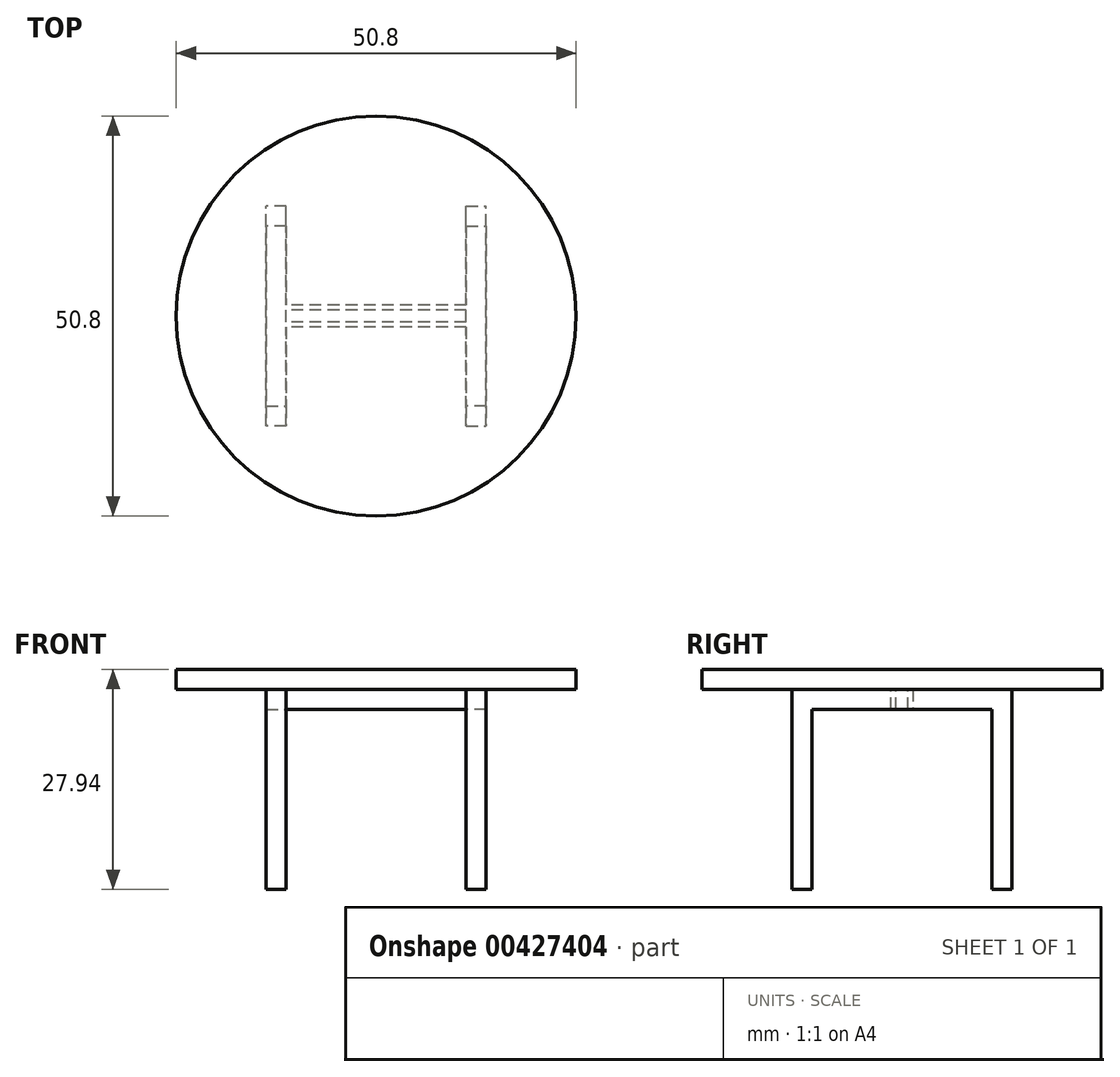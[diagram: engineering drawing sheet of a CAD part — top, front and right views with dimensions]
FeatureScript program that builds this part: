
annotation { "Feature Type Name" : "Feature", "Feature Type Description" : "" }
export const myFeature = defineFeature(function(context is Context, id is Id, definition is map)
    precondition{}
    {
        {
            var Q0;
            Q0=qCreatedBy(makeId("Top.planeOp"),FACE);
            var sketch = newSketch(context, id + "F0", { "sketchPlane" : qUnion([Q0])});
            skCircle(sketch, "E0", {"center": v(0, 0) * mm, "radius": 25.4 * mm});
            skSolve(sketch);
        }
        {
            var Q0;
            Q0 = qSketchRegion(id + "F0", true);
            extrude(context, id + "F1", {"entities" : qUnion([Q0]), "depth" : 2.54 * mm});
        }
        {
            var Q0;
            Q0=makeQuery(id+"F1.opExtrude","CAP_FACE",FACE,{"disambiguationData":[OSD([sQuery(id+"F0.wireOp",EDGE,"E0")])],"isStart":true});
            var sketch = newSketch(context, id + "F2", { "sketchPlane" : qUnion([Q0])});
            skLineSegment(sketch, "E1.bottom", {"start": v(11.43, -11.43) * mm, "end": v(13.97, -11.43) * mm});
            skLineSegment(sketch, "E1.top", {"start": v(11.43, -13.97) * mm, "end": v(13.97, -13.97) * mm});
            skLineSegment(sketch, "E1.left", {"start": v(11.43, -11.43) * mm, "end": v(11.43, -13.97) * mm});
            skLineSegment(sketch, "E1.right", {"start": v(13.97, -11.43) * mm, "end": v(13.97, -13.97) * mm});
            skPoint(sketch, "E1.middle", {"position": v(12.7, -12.7) * mm});
            skLineSegment(sketch, "E2.MirrorCS", {"start": v(-11.43, -13.97) * mm, "end": v(-13.97, -13.97) * mm});
            skLineSegment(sketch, "E3.MirrorCS", {"start": v(-13.97, -11.43) * mm, "end": v(-13.97, -13.97) * mm});
            skLineSegment(sketch, "E4.MirrorCS", {"start": v(-11.43, -11.43) * mm, "end": v(-13.97, -11.43) * mm});
            skLineSegment(sketch, "E5.MirrorCS", {"start": v(-11.43, -11.43) * mm, "end": v(-11.43, -13.97) * mm});
            skLineSegment(sketch, "E6.MirrorCS", {"start": v(-11.43, 11.43) * mm, "end": v(-13.97, 11.43) * mm});
            skLineSegment(sketch, "E7.MirrorCS", {"start": v(-11.43, 11.43) * mm, "end": v(-11.43, 13.97) * mm});
            skLineSegment(sketch, "E8.MirrorCS", {"start": v(-11.43, 13.97) * mm, "end": v(-13.97, 13.97) * mm});
            skLineSegment(sketch, "E9.MirrorCS", {"start": v(-13.97, 11.43) * mm, "end": v(-13.97, 13.97) * mm});
            skLineSegment(sketch, "E10.MirrorCS", {"start": v(11.43, 13.97) * mm, "end": v(13.97, 13.97) * mm});
            skLineSegment(sketch, "E11.MirrorCS", {"start": v(13.97, 11.43) * mm, "end": v(13.97, 13.97) * mm});
            skLineSegment(sketch, "E12.MirrorCS", {"start": v(11.43, 11.43) * mm, "end": v(13.97, 11.43) * mm});
            skLineSegment(sketch, "E13.MirrorCS", {"start": v(11.43, 11.43) * mm, "end": v(11.43, 13.97) * mm});
            skSolve(sketch);
        }
        {
            var Q0;
            Q0 = qSketchRegion(id + "F2", true);
            extrude(context, id + "F3", {"entities" : qUnion([Q0]), "operationType" : NewBodyOperationType.ADD, "depth" : 25.4 * mm});
        }
        {
            var Q0;
            Q0=makeQuery(id+"F3.opExtrude","SWEPT_FACE",FACE,{"disambiguationData":[OSD([sQuery(id+"F2.wireOp",EDGE,"E6.MirrorCS")])]});
            var sketch = newSketch(context, id + "F4", { "sketchPlane" : qUnion([Q0])});
            skLineSegment(sketch, "E14.bottom", {"start": v(13.97, 0) * mm, "end": v(11.43, 0) * mm});
            skLineSegment(sketch, "E14.top", {"start": v(13.97, -2.54) * mm, "end": v(11.43, -2.54) * mm});
            skLineSegment(sketch, "E14.left", {"start": v(13.97, 0) * mm, "end": v(13.97, -2.54) * mm});
            skLineSegment(sketch, "E14.right", {"start": v(11.43, 0) * mm, "end": v(11.43, -2.54) * mm});
            skSolve(sketch);
        }
        {
            var Q0;
            Q0 = qSketchRegion(id + "F4", true);
            extrude(context, id + "F5", {"entities" : qUnion([Q0]), "operationType" : NewBodyOperationType.ADD, "depth" : 25.4 * mm});
        }
        {
            var Q0;
            Q0=makeQuery(id+"F1.opExtrude","SWEPT_BODY",BODY,{"disambiguationData":[OSD([sQuery(id+"F0.wireOp",EDGE,"E0")])]});
            var Q1;
            Q1=qCreatedBy(makeId("Right.planeOp"),FACE);
            mirror(context, id + "F6", {"operationType" : NewBodyOperationType.ADD, "entities" : qUnion([Q0]), "mirrorPlane" : qUnion([Q1])});
        }
        {
            var Q0;
            Q0=makeQuery(id+"F5.boolean.opBoolean","MERGE",FACE,{"derivedFrom":[makeQuery(id+"F3.opExtrude","SWEPT_FACE",FACE,{"disambiguationData":[OSD([sQuery(id+"F2.wireOp",EDGE,"E5.MirrorCS")])]}),makeQuery(id+"F3.opExtrude","SWEPT_FACE",FACE,{"disambiguationData":[OSD([sQuery(id+"F2.wireOp",EDGE,"E7.MirrorCS")])]}),makeQuery(id+"F5.opExtrude","SWEPT_FACE",FACE,{"disambiguationData":[OSD([sQuery(id+"F4.wireOp",EDGE,"E14.right")])]})]});
            var sketch = newSketch(context, id + "F7", { "sketchPlane" : qUnion([Q0])});
            skLineSegment(sketch, "E15", {"start": v(0, -2.54) * mm, "end": v(-0.76, -2.54) * mm});
            skLineSegment(sketch, "E16.bottom", {"start": v(-0.76, -2.54) * mm, "end": v(-1.4, -2.54) * mm});
            skLineSegment(sketch, "E16.top", {"start": v(-0.76, 0) * mm, "end": v(-1.4, 0) * mm});
            skLineSegment(sketch, "E16.left", {"start": v(-0.76, -2.54) * mm, "end": v(-0.76, 0) * mm});
            skLineSegment(sketch, "E16.right", {"start": v(-1.4, -2.54) * mm, "end": v(-1.4, 0) * mm});
            skSolve(sketch);
        }
        {
            var Q0;
            Q0 = qSketchRegion(id + "F7", true);
            extrude(context, id + "F8", {"entities" : qUnion([Q0]), "operationType" : NewBodyOperationType.ADD, "depth" : 25.4 * mm});
        }
        {
            var Q0;
            Q0=makeQuery(id+"F1.opExtrude","SWEPT_BODY",BODY,{"disambiguationData":[OSD([sQuery(id+"F0.wireOp",EDGE,"E0")])]});
            var Q1;
            Q1=qCreatedBy(makeId("Front.planeOp"),FACE);
            mirror(context, id + "F9", {"operationType" : NewBodyOperationType.ADD, "entities" : qUnion([Q0]), "mirrorPlane" : qUnion([Q1])});
        }
    });
